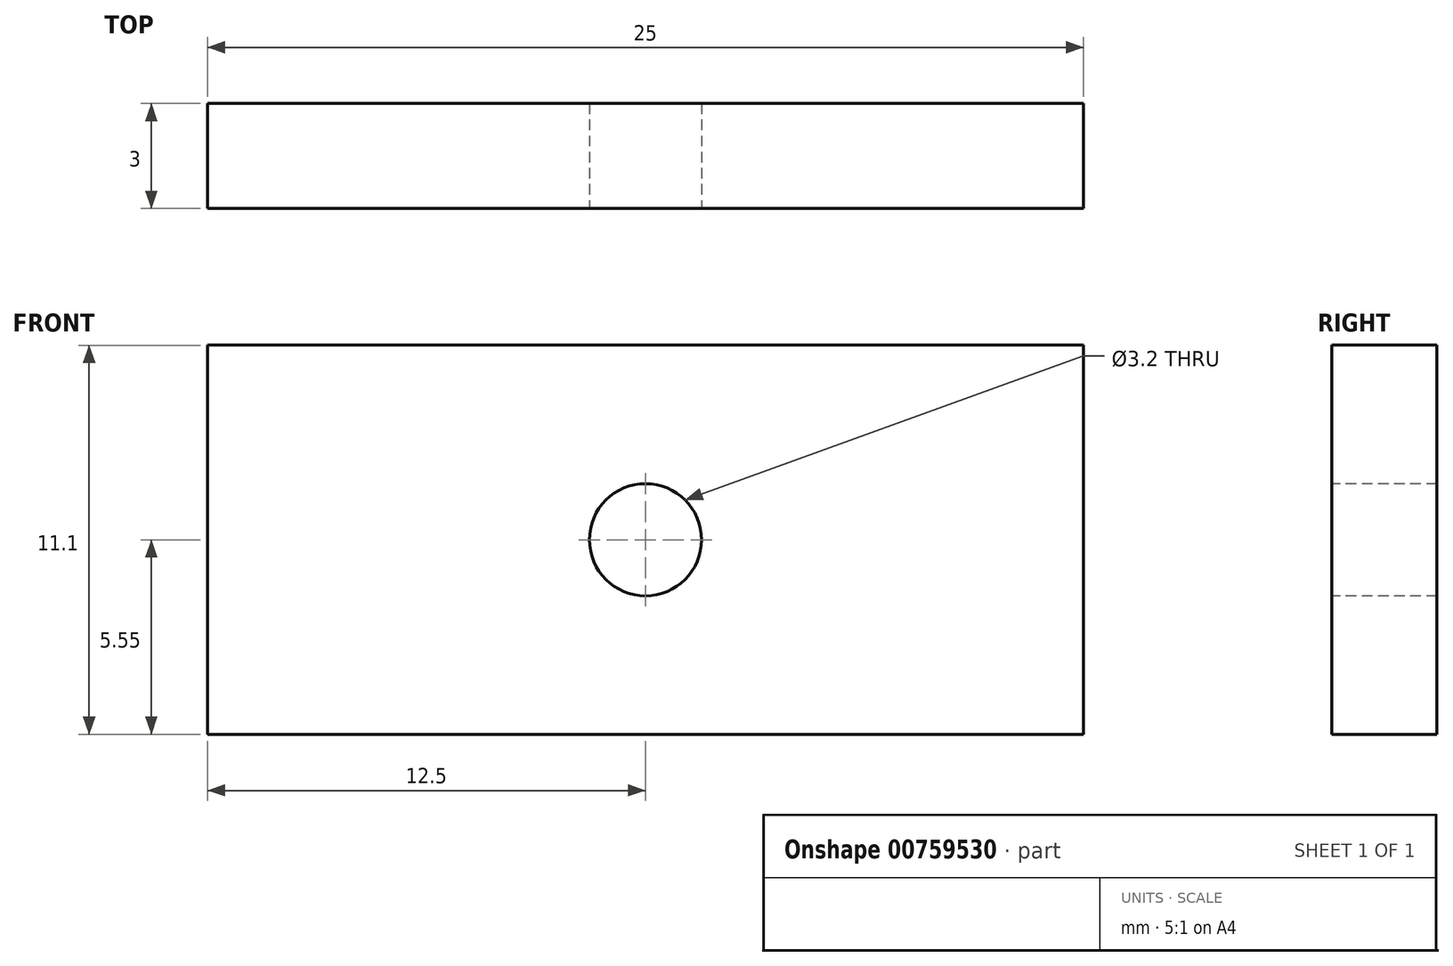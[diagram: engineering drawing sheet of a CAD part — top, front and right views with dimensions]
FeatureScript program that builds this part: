
annotation { "Feature Type Name" : "Feature", "Feature Type Description" : "" }
export const myFeature = defineFeature(function(context is Context, id is Id, definition is map)
    precondition{}
    {
        {
            var Q0;
            Q0=qCreatedBy(makeId("Front.planeOp"),FACE);
            var sketch = newSketch(context, id + "F0", { "sketchPlane" : qUnion([Q0])});
            skLineSegment(sketch, "E0.bottom", {"start": v(12.5, 5.56) * mm, "end": v(-12.5, 5.55) * mm});
            skLineSegment(sketch, "E0.top", {"start": v(12.5, -5.55) * mm, "end": v(-12.5, -5.56) * mm});
            skLineSegment(sketch, "E0.left", {"start": v(12.5, 5.56) * mm, "end": v(12.5, -5.55) * mm});
            skLineSegment(sketch, "E0.right", {"start": v(-12.5, 5.55) * mm, "end": v(-12.5, -5.56) * mm});
            skPoint(sketch, "E0.middle", {"position": v(0, 0) * mm});
            skCircle(sketch, "E1", {"center": v(0, 0) * mm, "radius": 1.6 * mm});
            skSolve(sketch);
        }
        {
            var Q0;
            Q0 = qSketchRegion(id + "F0", true);
            extrude(context, id + "F1", {"entities" : qUnion([Q0]), "oppositeDirection" : true, "depth" : 3 * mm, "offsetDistance" : 25 * mm});
        }
    });
